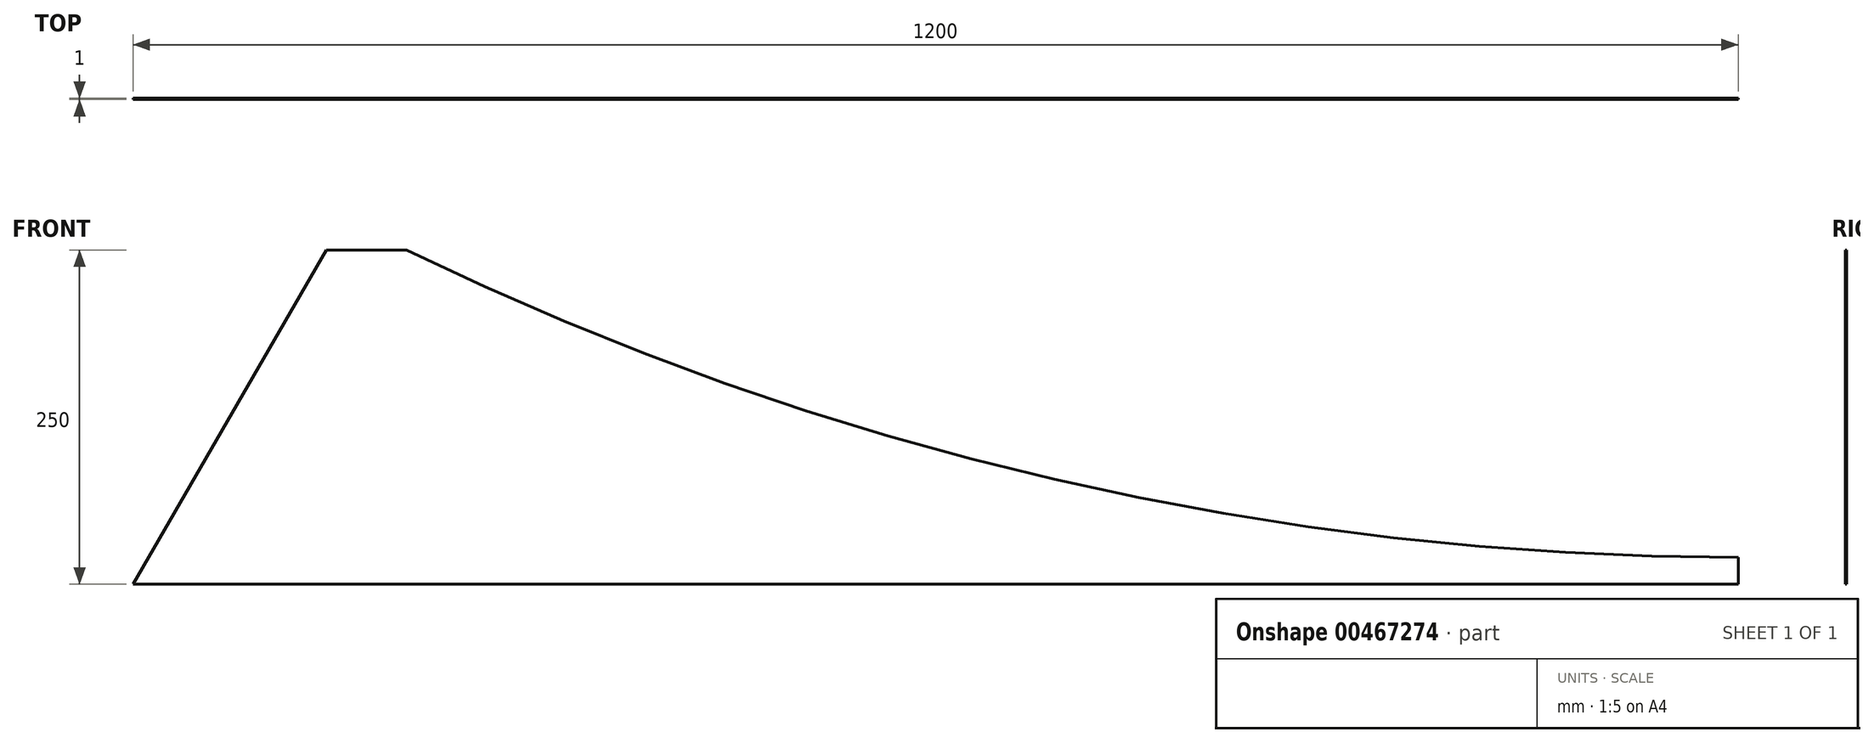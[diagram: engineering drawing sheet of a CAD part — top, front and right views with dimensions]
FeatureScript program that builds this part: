
annotation { "Feature Type Name" : "Feature", "Feature Type Description" : "" }
export const myFeature = defineFeature(function(context is Context, id is Id, definition is map)
    precondition{}
    {
        {
            var Q0;
            Q0=qCreatedBy(makeId("Front.planeOp"),FACE);
            var sketch = newSketch(context, id + "F0", { "sketchPlane" : qUnion([Q0])});
            skLineSegment(sketch, "E0", {"start": v(0, 0) * mm, "end": v(1200, 0) * mm});
            skLineSegment(sketch, "E1", {"start": v(1200, 0) * mm, "end": v(1200, 20) * mm});
            skLineSegment(sketch, "E2", {"start": v(1200, 20) * mm, "end": v(1200, 20) * mm});
            skLineSegment(sketch, "E3", {"start": v(204.34, 250) * mm, "end": v(144.34, 250) * mm});
            skLineSegment(sketch, "E4", {"start": v(144.34, 250) * mm, "end": v(0, 0) * mm});
            skPoint(sketch, "E5.visualSharp", {"position": v(337.13, 20) * mm});
            skArc(sketch, "E5.filletArc", {"start": v(204.34, 250) * mm, "mid": v(689.06, 78.25) * mm, "end": v(1200, 20) * mm});
            skSolve(sketch);
        }
        {
            var Q0;
            Q0=makeQuery(id+"F0.imprint","IMPRINT",FACE,{"disambiguationData":[TD([[makeQuery(id+"F0.imprint","IMPRINT",EDGE,{"derivedFrom":sQuery(id+"F0.wireOp",EDGE,"E0")}),1.0]])]});
            extrude(context, id + "F1", {"entities" : qUnion([Q0]), "depth" : 1 * mm});
        }
    });
